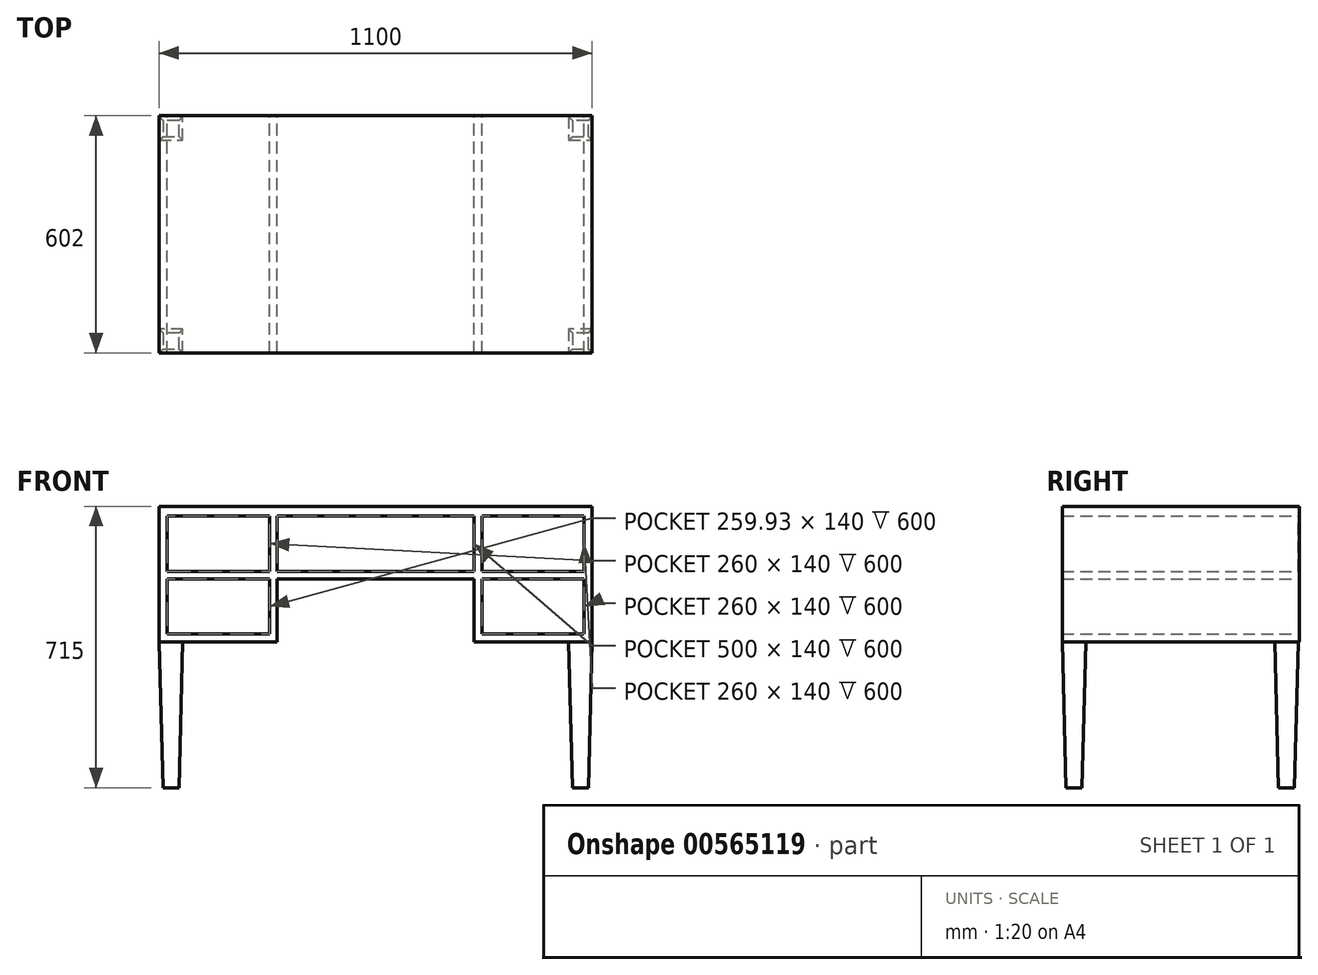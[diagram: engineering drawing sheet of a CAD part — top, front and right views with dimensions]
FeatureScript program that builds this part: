
annotation { "Feature Type Name" : "Feature", "Feature Type Description" : "" }
export const myFeature = defineFeature(function(context is Context, id is Id, definition is map)
    precondition{}
    {
        {
            var Q0;
            Q0=qCreatedBy(makeId("Front.planeOp"),FACE);
            var sketch = newSketch(context, id + "F0", { "sketchPlane" : qUnion([Q0])});
            skLineSegment(sketch, "E0", {"start": v(-550, 172.5) * mm, "end": v(-550, -172.5) * mm});
            skLineSegment(sketch, "E1", {"start": v(-500.12, -172.5) * mm, "end": v(-550, -172.5) * mm});
            skLineSegment(sketch, "E2", {"start": v(-250, -172.5) * mm, "end": v(-500.12, -172.5) * mm});
            skLineSegment(sketch, "E3", {"start": v(-250, -172.5) * mm, "end": v(-250, -12.5) * mm});
            skLineSegment(sketch, "E4", {"start": v(250, -12.5) * mm, "end": v(-250, -12.5) * mm});
            skLineSegment(sketch, "E5", {"start": v(250, -172.5) * mm, "end": v(250, -12.5) * mm});
            skLineSegment(sketch, "E6", {"start": v(490, -172.5) * mm, "end": v(250, -172.5) * mm});
            skLineSegment(sketch, "E7", {"start": v(550, -172.5) * mm, "end": v(490, -172.5) * mm});
            skLineSegment(sketch, "E8", {"start": v(550, 172.5) * mm, "end": v(550, -172.5) * mm});
            skLineSegment(sketch, "E9", {"start": v(550, 172.5) * mm, "end": v(-550, 172.5) * mm});
            skLineSegment(sketch, "E10", {"start": v(-530, -12.5) * mm, "end": v(-530, -152.5) * mm});
            skLineSegment(sketch, "E11", {"start": v(-270.07, -12.5) * mm, "end": v(-530, -12.5) * mm});
            skLineSegment(sketch, "E12", {"start": v(-270.07, -12.5) * mm, "end": v(-270.07, -152.5) * mm});
            skLineSegment(sketch, "E13", {"start": v(-270.07, -152.5) * mm, "end": v(-530, -152.5) * mm});
            skLineSegment(sketch, "E14", {"start": v(530, 147.5) * mm, "end": v(530, 7.5) * mm});
            skLineSegment(sketch, "E15", {"start": v(530, 7.5) * mm, "end": v(270, 7.5) * mm});
            skLineSegment(sketch, "E16", {"start": v(270, 147.5) * mm, "end": v(270, 7.5) * mm});
            skLineSegment(sketch, "E17", {"start": v(530, 147.5) * mm, "end": v(270, 147.5) * mm});
            skLineSegment(sketch, "E18", {"start": v(250, 147.5) * mm, "end": v(250, 7.5) * mm});
            skLineSegment(sketch, "E19", {"start": v(250, 7.5) * mm, "end": v(-250, 7.5) * mm});
            skLineSegment(sketch, "E20", {"start": v(-250, 147.5) * mm, "end": v(-250, 7.5) * mm});
            skLineSegment(sketch, "E21", {"start": v(250, 147.5) * mm, "end": v(-250, 147.5) * mm});
            skLineSegment(sketch, "E22", {"start": v(-270, 7.5) * mm, "end": v(-270, 147.5) * mm});
            skLineSegment(sketch, "E23", {"start": v(-270, 7.5) * mm, "end": v(-530, 7.5) * mm});
            skLineSegment(sketch, "E24", {"start": v(-530, 7.5) * mm, "end": v(-530, 147.5) * mm});
            skLineSegment(sketch, "E25", {"start": v(-270, 147.5) * mm, "end": v(-530, 147.5) * mm});
            skLineSegment(sketch, "E26", {"start": v(270, -12.5) * mm, "end": v(270, -152.5) * mm});
            skLineSegment(sketch, "E27", {"start": v(530, -12.5) * mm, "end": v(270, -12.5) * mm});
            skLineSegment(sketch, "E28", {"start": v(530, -12.5) * mm, "end": v(530, -152.5) * mm});
            skLineSegment(sketch, "E29", {"start": v(530, -152.5) * mm, "end": v(270, -152.5) * mm});
            skSolve(sketch);
        }
        {
            var Q0;
            Q0=qCreatedBy(makeId("Front.planeOp"),FACE);
            var sketch = newSketch(context, id + "F1", { "sketchPlane" : qUnion([Q0])});
            skLineSegment(sketch, "E30", {"start": v(550, 172.5) * mm, "end": v(550, -172.5) * mm});
            skLineSegment(sketch, "E31", {"start": v(550, 172.5) * mm, "end": v(-550, 172.5) * mm});
            skLineSegment(sketch, "E32", {"start": v(-550, 172.5) * mm, "end": v(-550, -172.5) * mm});
            skLineSegment(sketch, "E33", {"start": v(-250, -172.5) * mm, "end": v(-550, -172.5) * mm});
            skLineSegment(sketch, "E34", {"start": v(-250, -172.5) * mm, "end": v(-250, -12.5) * mm});
            skLineSegment(sketch, "E35", {"start": v(250, -12.5) * mm, "end": v(-250, -12.5) * mm});
            skLineSegment(sketch, "E36", {"start": v(250, -172.5) * mm, "end": v(250, -12.5) * mm});
            skLineSegment(sketch, "E37", {"start": v(550, -172.5) * mm, "end": v(250, -172.5) * mm});
            skSolve(sketch);
        }
        {
            var Q0;
            Q0=makeQuery(id+"F0.imprint","IMPRINT",FACE,{"disambiguationData":[TD([[makeQuery(id+"F0.imprint","IMPRINT",EDGE,{"derivedFrom":sQuery(id+"F0.wireOp",EDGE,"E0")}),1.0]])]});
            extrude(context, id + "F2", {"entities" : qUnion([Q0]), "depth" : 600 * mm, "offsetDistance" : 25 * mm});
        }
        {
            var Q0;
            Q0 = qSketchRegion(id + "F1", true);
            extrude(context, id + "F3", {"entities" : qUnion([Q0]), "operationType" : NewBodyOperationType.ADD, "oppositeDirection" : true, "depth" : 2 * mm, "offsetDistance" : 25 * mm});
        }
        {
            var Q0;
            Q0=makeQuery(id+"F3.boolean.opBoolean","MERGE",FACE,{"derivedFrom":[makeQuery(id+"F2.opExtrude","SWEPT_FACE",FACE,{"disambiguationData":[OSD([sQuery(id+"F0.wireOp",EDGE,"E1"),sQuery(id+"F0.wireOp",EDGE,"E2")])]}),makeQuery(id+"F3.opExtrude","SWEPT_FACE",FACE,{"disambiguationData":[OSD([sQuery(id+"F1.wireOp",EDGE,"E33")])]})]});
            var sketch = newSketch(context, id + "F4", { "sketchPlane" : qUnion([Q0])});
            skLineSegment(sketch, "E38.bottom", {"start": v(-550, 600) * mm, "end": v(-490, 600) * mm});
            skLineSegment(sketch, "E38.top", {"start": v(-550, 540) * mm, "end": v(-490, 540) * mm});
            skLineSegment(sketch, "E38.left", {"start": v(-550, 600) * mm, "end": v(-550, 540) * mm});
            skLineSegment(sketch, "E38.right", {"start": v(-490, 600) * mm, "end": v(-490, 540) * mm});
            skLineSegment(sketch, "E39.bottom", {"start": v(-550, 0) * mm, "end": v(-490, 0) * mm});
            skLineSegment(sketch, "E39.top", {"start": v(-550, 60) * mm, "end": v(-490, 60) * mm});
            skLineSegment(sketch, "E39.left", {"start": v(-550, 0) * mm, "end": v(-550, 60) * mm});
            skLineSegment(sketch, "E39.right", {"start": v(-490, 0) * mm, "end": v(-490, 60) * mm});
            skSolve(sketch);
        }
        {
            var Q0;
            Q0=makeQuery(id+"F3.boolean.opBoolean","MERGE",FACE,{"derivedFrom":[makeQuery(id+"F2.opExtrude","SWEPT_FACE",FACE,{"disambiguationData":[OSD([sQuery(id+"F0.wireOp",EDGE,"E6"),sQuery(id+"F0.wireOp",EDGE,"E7")])]}),makeQuery(id+"F3.opExtrude","SWEPT_FACE",FACE,{"disambiguationData":[OSD([sQuery(id+"F1.wireOp",EDGE,"E37")])]})]});
            var sketch = newSketch(context, id + "F5", { "sketchPlane" : qUnion([Q0])});
            skLineSegment(sketch, "E40.bottom", {"start": v(550, 600) * mm, "end": v(490, 600) * mm});
            skLineSegment(sketch, "E40.top", {"start": v(550, 540) * mm, "end": v(490, 540) * mm});
            skLineSegment(sketch, "E40.left", {"start": v(550, 600) * mm, "end": v(550, 540) * mm});
            skLineSegment(sketch, "E40.right", {"start": v(490, 600) * mm, "end": v(490, 540) * mm});
            skLineSegment(sketch, "E41.bottom", {"start": v(550, 0) * mm, "end": v(490, 0) * mm});
            skLineSegment(sketch, "E41.top", {"start": v(550, 60) * mm, "end": v(490, 60) * mm});
            skLineSegment(sketch, "E41.left", {"start": v(550, 0) * mm, "end": v(550, 60) * mm});
            skLineSegment(sketch, "E41.right", {"start": v(490, 0) * mm, "end": v(490, 60) * mm});
            skSolve(sketch);
        }
        {
            var Q0;
            Q0=makeQuery(id+"F4.imprint","IMPRINT",FACE,{"disambiguationData":[TD([[makeQuery(id+"F4.imprint","IMPRINT",EDGE,{"derivedFrom":sQuery(id+"F4.wireOp",EDGE,"E38.bottom")}),1.0]])]});
            var Q1;
            Q1=makeQuery(id+"F4.imprint","IMPRINT",FACE,{"disambiguationData":[TD([[makeQuery(id+"F4.imprint","IMPRINT",EDGE,{"derivedFrom":sQuery(id+"F4.wireOp",EDGE,"E39.bottom")}),1.0]])]});
            var Q2;
            Q2=makeQuery(id+"F5.imprint","IMPRINT",FACE,{"disambiguationData":[TD([[makeQuery(id+"F5.imprint","IMPRINT",EDGE,{"derivedFrom":sQuery(id+"F5.wireOp",EDGE,"E40.bottom")}),1.0]])]});
            var Q3;
            Q3=makeQuery(id+"F5.imprint","IMPRINT",FACE,{"disambiguationData":[TD([[makeQuery(id+"F5.imprint","IMPRINT",EDGE,{"derivedFrom":sQuery(id+"F5.wireOp",EDGE,"E41.bottom")}),-1.0]])]});
            extrude(context, id + "F6", {"entities" : qUnion([Q0, Q1, Q2, Q3]), "operationType" : NewBodyOperationType.ADD, "depth" : 370 * mm, "offsetDistance" : 25 * mm, "hasDraft" : true, "draftAngle" : 1.5 * degree, "draftPullDirection" : true});
        }
    });
